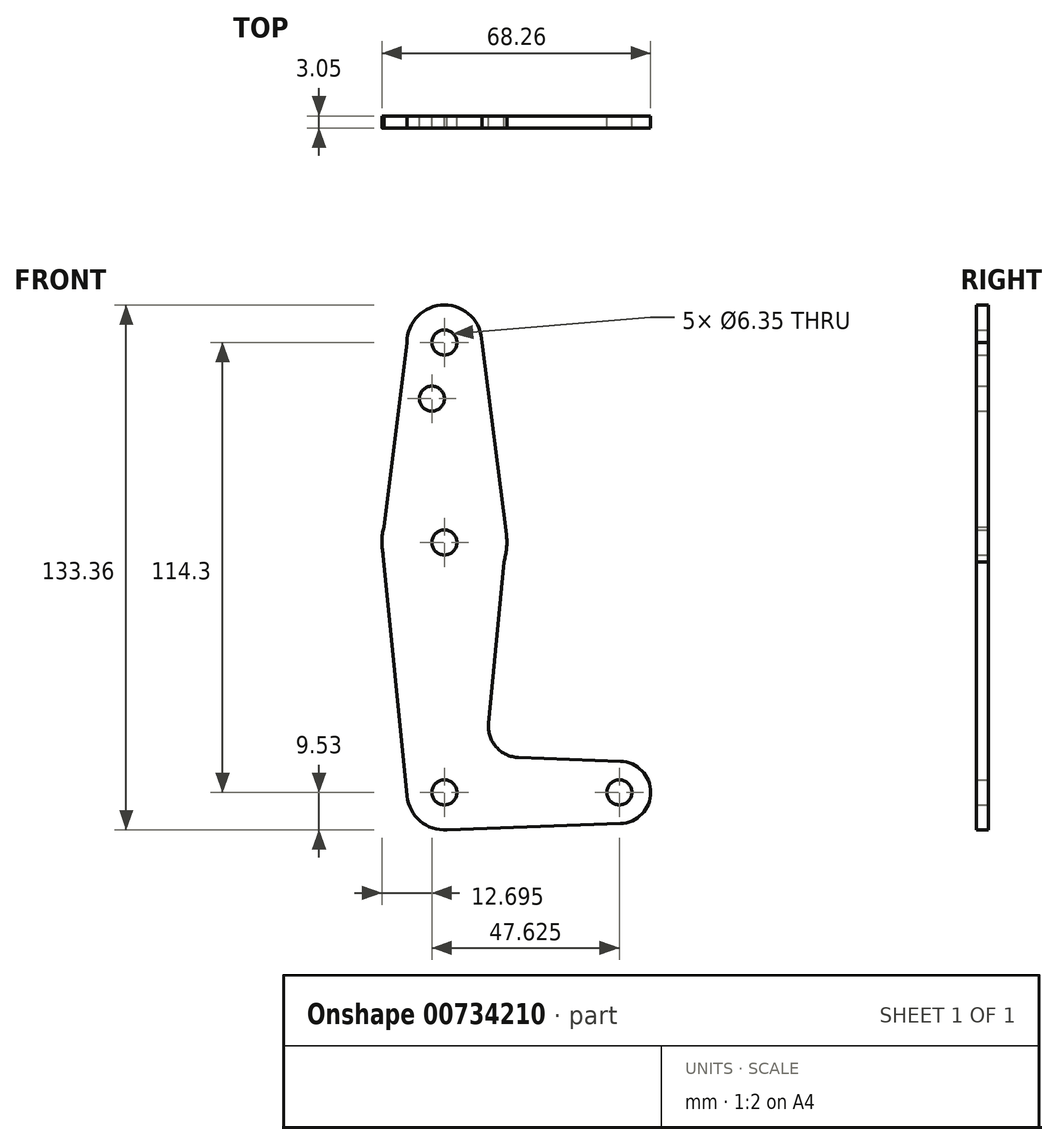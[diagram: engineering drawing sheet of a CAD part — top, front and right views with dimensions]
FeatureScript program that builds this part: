
annotation { "Feature Type Name" : "Feature", "Feature Type Description" : "" }
export const myFeature = defineFeature(function(context is Context, id is Id, definition is map)
    precondition{}
    {
        {
            var Q0;
            Q0=qCreatedBy(makeId("Front.planeOp"),FACE);
            var sketch = newSketch(context, id + "F0", { "sketchPlane" : qUnion([Q0])});
            skLineSegment(sketch, "E0", {"start": v(0, 0) * mm, "end": v(44.45, 0) * mm, "construction": true});
            skLineSegment(sketch, "E1", {"start": v(0, 0) * mm, "end": v(0, 114.3) * mm, "construction": true});
            skCircle(sketch, "E2", {"center": v(0, 63.5) * mm, "radius": 15.88 * mm});
            skCircle(sketch, "E3", {"center": v(0, 0) * mm, "radius": 9.53 * mm});
            skCircle(sketch, "E4", {"center": v(0, 114.3) * mm, "radius": 9.53 * mm});
            skCircle(sketch, "E5", {"center": v(44.45, 0) * mm, "radius": 7.94 * mm});
            skPoint(sketch, "E6", {"position": v(0, 57.15) * mm});
            skLineSegment(sketch, "E7", {"start": v(-9.53, 114.3) * mm, "end": v(-15.88, 63.5) * mm});
            skLineSegment(sketch, "E8", {"start": v(9.53, 114.3) * mm, "end": v(15.75, 65.5) * mm});
            skLineSegment(sketch, "E9", {"start": v(15.75, 65.5) * mm, "end": v(11.22, 17.55) * mm});
            skLineSegment(sketch, "E10", {"start": v(-15.88, 63.5) * mm, "end": v(-9.48, -0.94) * mm});
            skLineSegment(sketch, "E11", {"start": v(18.85, 8.85) * mm, "end": v(44.73, 7.93) * mm});
            skLineSegment(sketch, "E12", {"start": v(0, -9.53) * mm, "end": v(44.73, -7.93) * mm});
            skCircle(sketch, "E13", {"center": v(0, 114.3) * mm, "radius": 3.18 * mm});
            skCircle(sketch, "E14", {"center": v(0, 63.5) * mm, "radius": 3.18 * mm});
            skCircle(sketch, "E15", {"center": v(0, 0) * mm, "radius": 3.18 * mm});
            skCircle(sketch, "E16", {"center": v(44.45, 0) * mm, "radius": 3.18 * mm});
            skCircle(sketch, "E17", {"center": v(-3.18, 100.03) * mm, "radius": 3.18 * mm});
            skPoint(sketch, "E18.newPointB", {"position": v(0, 9.53) * mm});
            skArc(sketch, "E18.filletArc", {"start": v(11.22, 17.55) * mm, "mid": v(13.16, 11.55) * mm, "end": v(18.85, 8.85) * mm});
            skSolve(sketch);
        }
        {
            var Q0;
            Q0 = qSketchRegion(id + "F0", true);
            extrude(context, id + "F1", {"entities" : qUnion([Q0]), "depth" : 3.05 * mm, "offsetDistance" : 25.4 * mm});
        }
    });
